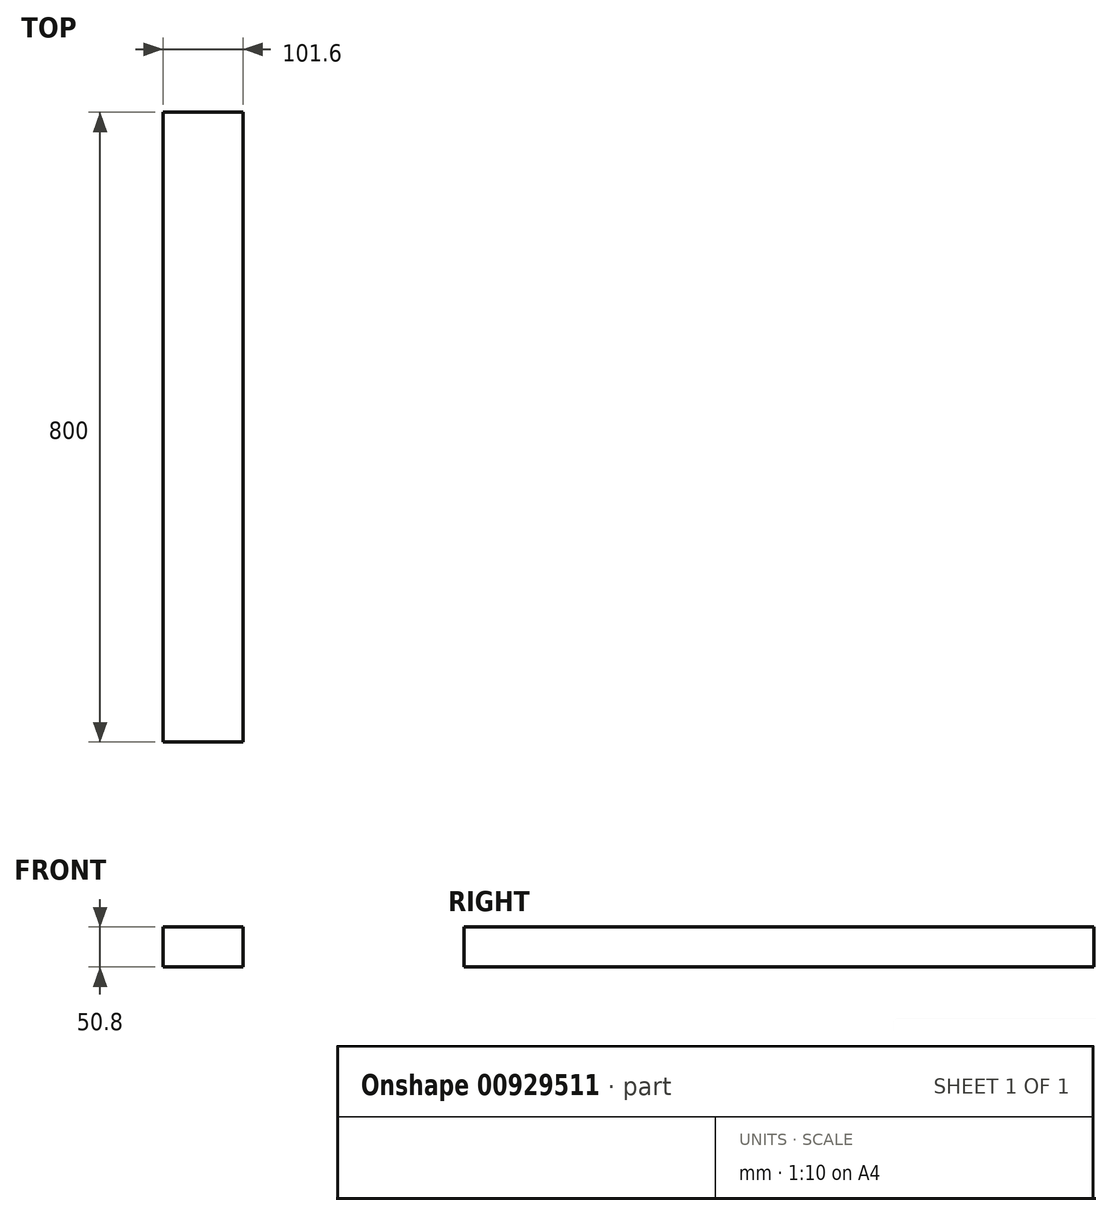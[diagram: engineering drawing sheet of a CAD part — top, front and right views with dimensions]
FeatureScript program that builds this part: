
annotation { "Feature Type Name" : "Feature", "Feature Type Description" : "" }
export const myFeature = defineFeature(function(context is Context, id is Id, definition is map)
    precondition{}
    {
        {
            var Q0;
            Q0=qCreatedBy(makeId("Front.planeOp"),FACE);
            var sketch = newSketch(context, id + "F0", { "sketchPlane" : qUnion([Q0])});
            skLineSegment(sketch, "E0", {"start": v(0, 0) * mm, "end": v(50.8, 0) * mm});
            skLineSegment(sketch, "E1", {"start": v(0, 0) * mm, "end": v(-50.8, 0) * mm});
            skLineSegment(sketch, "E2", {"start": v(50.8, 0) * mm, "end": v(50.8, 50.8) * mm});
            skLineSegment(sketch, "E3", {"start": v(-50.8, 0) * mm, "end": v(-50.8, 50.8) * mm});
            skLineSegment(sketch, "E4", {"start": v(-50.8, 50.8) * mm, "end": v(50.8, 50.8) * mm});
            skSolve(sketch);
        }
        {
            var Q0;
            Q0=makeQuery(id+"F0.imprint","IMPRINT",FACE,{"disambiguationData":[TD([[makeQuery(id+"F0.imprint","IMPRINT",EDGE,{"derivedFrom":sQuery(id+"F0.wireOp",EDGE,"E0")}),1.0]])]});
            extrude(context, id + "F1", {"entities" : qUnion([Q0]), "endBound" : BoundingType.SYMMETRIC, "depth" : 800 * mm, "offsetDistance" : 25 * mm});
        }
    });
